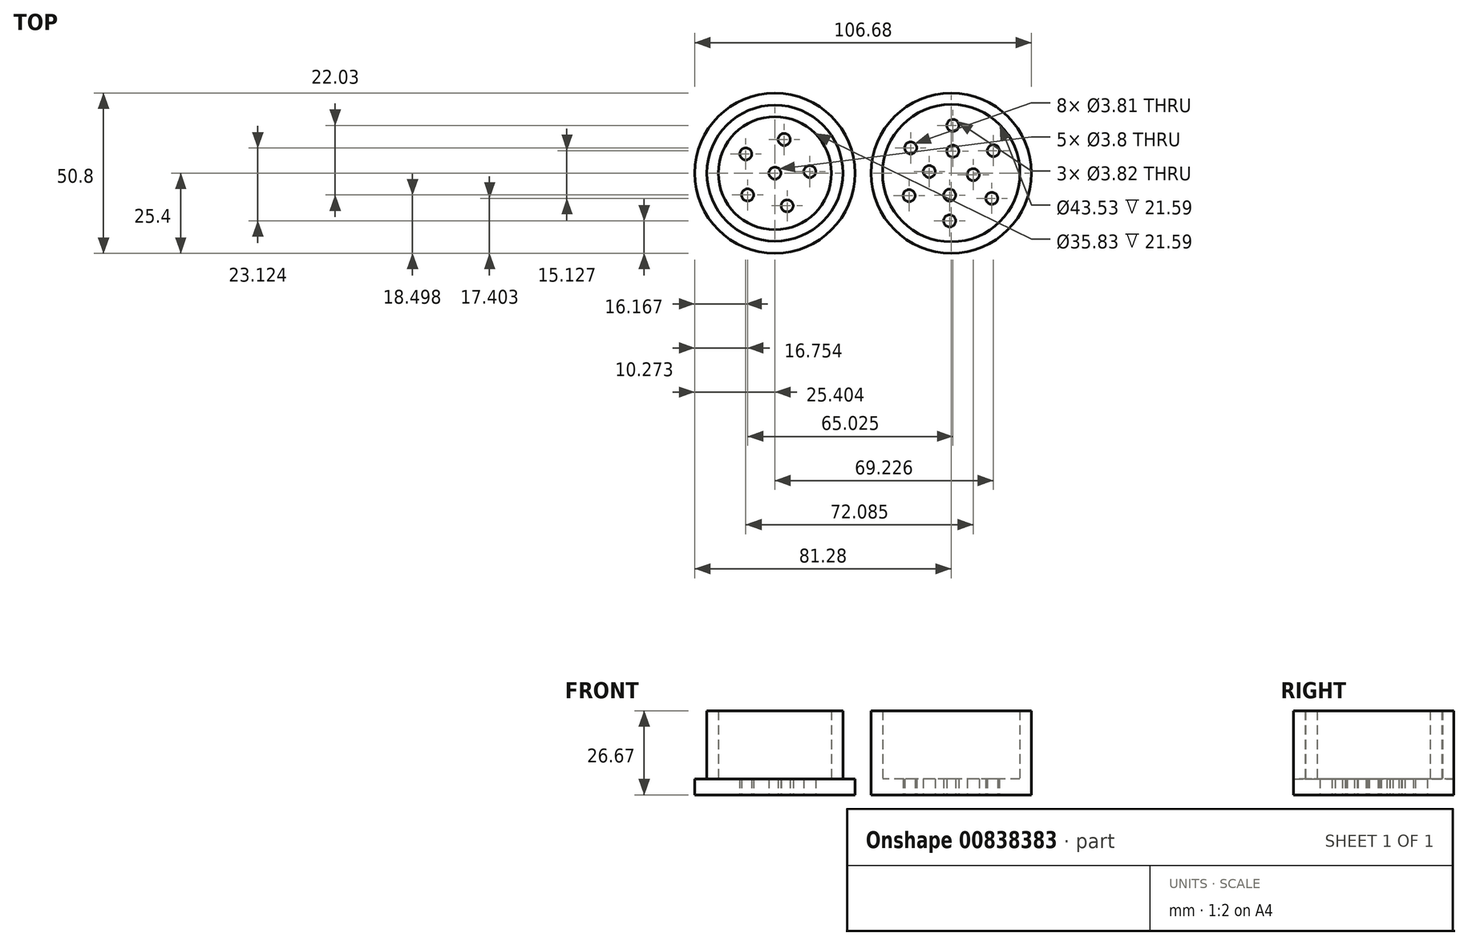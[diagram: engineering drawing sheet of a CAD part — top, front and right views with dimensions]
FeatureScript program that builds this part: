
annotation { "Feature Type Name" : "Feature", "Feature Type Description" : "" }
export const myFeature = defineFeature(function(context is Context, id is Id, definition is map)
    precondition{}
    {
        {
            var Q0;
            Q0=qCreatedBy(makeId("Top.planeOp"),FACE);
            var sketch = newSketch(context, id + "F0", { "sketchPlane" : qUnion([Q0])});
            skCircle(sketch, "E0", {"center": v(0, 0) * mm, "radius": 25.4 * mm});
            skCircle(sketch, "E1", {"center": v(0, 0) * mm, "radius": 21.77 * mm});
            skCircle(sketch, "E2", {"center": v(0, 0) * mm, "radius": 15.14 * mm});
            skCircle(sketch, "E3.cCircle", {"center": v(0, 0) * mm, "radius": 15.14 * mm, "construction": true});
            skLineSegment(sketch, "E3.0", {"start": v(0.5, 15.13) * mm, "end": v(13.35, 7.13) * mm});
            skLineSegment(sketch, "E3.1", {"start": v(13.35, 7.13) * mm, "end": v(12.85, -8) * mm});
            skLineSegment(sketch, "E3.2", {"start": v(12.85, -8) * mm, "end": v(-0.5, -15.13) * mm});
            skLineSegment(sketch, "E3.3", {"start": v(-0.5, -15.13) * mm, "end": v(-13.35, -7.13) * mm});
            skLineSegment(sketch, "E3.4", {"start": v(-13.35, -7.13) * mm, "end": v(-12.85, 8) * mm});
            skLineSegment(sketch, "E3.5", {"start": v(-12.85, 8) * mm, "end": v(0.5, 15.13) * mm});
            skCircle(sketch, "E4", {"center": v(0.5, 15.13) * mm, "radius": 1.9 * mm});
            skCircle(sketch, "E5", {"center": v(-12.85, 8) * mm, "radius": 1.9 * mm});
            skCircle(sketch, "E6", {"center": v(-13.35, -7.13) * mm, "radius": 1.9 * mm});
            skCircle(sketch, "E7", {"center": v(-0.5, -15.13) * mm, "radius": 1.9 * mm});
            skCircle(sketch, "E8", {"center": v(12.85, -8) * mm, "radius": 1.9 * mm});
            skCircle(sketch, "E9", {"center": v(13.35, 7.13) * mm, "radius": 1.9 * mm});
            skCircle(sketch, "E10", {"center": v(-55.88, 0) * mm, "radius": 25.4 * mm});
            skCircle(sketch, "E11", {"center": v(-55.88, 0) * mm, "radius": 21.57 * mm});
            skCircle(sketch, "E12", {"center": v(-55.88, 0) * mm, "radius": 17.92 * mm});
            skCircle(sketch, "E13", {"center": v(0, 0) * mm, "radius": 17.04 * mm});
            skCircle(sketch, "E14", {"center": v(0, 0) * mm, "radius": 6.99 * mm});
            skCircle(sketch, "E15.cCircle", {"center": v(0, 0) * mm, "radius": 6.99 * mm, "construction": true});
            skLineSegment(sketch, "E15.0", {"start": v(0.5, 6.97) * mm, "end": v(6.97, -0.5) * mm});
            skLineSegment(sketch, "E15.1", {"start": v(6.97, -0.5) * mm, "end": v(-0.5, -6.97) * mm});
            skLineSegment(sketch, "E15.2", {"start": v(-0.5, -6.97) * mm, "end": v(-6.97, 0.5) * mm});
            skLineSegment(sketch, "E15.3", {"start": v(-6.97, 0.5) * mm, "end": v(0.5, 6.97) * mm});
            skCircle(sketch, "E16", {"center": v(0.5, 6.97) * mm, "radius": 1.9 * mm});
            skCircle(sketch, "E17", {"center": v(6.97, -0.5) * mm, "radius": 1.9 * mm});
            skCircle(sketch, "E18", {"center": v(-0.5, -6.97) * mm, "radius": 1.9 * mm});
            skCircle(sketch, "E19", {"center": v(-6.97, 0.5) * mm, "radius": 1.9 * mm});
            skCircle(sketch, "E20", {"center": v(-55.88, 0) * mm, "radius": 11.07 * mm});
            skCircle(sketch, "E21.cCircle", {"center": v(-55.88, 0) * mm, "radius": 11.07 * mm, "construction": true});
            skLineSegment(sketch, "E21.0", {"start": v(-44.82, 0.5) * mm, "end": v(-51.98, -10.36) * mm});
            skLineSegment(sketch, "E21.1", {"start": v(-51.98, -10.36) * mm, "end": v(-64.53, -6.9) * mm});
            skLineSegment(sketch, "E21.2", {"start": v(-64.53, -6.9) * mm, "end": v(-65.11, 6.1) * mm});
            skLineSegment(sketch, "E21.3", {"start": v(-65.11, 6.1) * mm, "end": v(-52.93, 10.67) * mm});
            skLineSegment(sketch, "E21.4", {"start": v(-52.93, 10.67) * mm, "end": v(-44.82, 0.5) * mm});
            skCircle(sketch, "E22", {"center": v(-64.53, -6.9) * mm, "radius": 1.9 * mm});
            skCircle(sketch, "E23", {"center": v(-51.98, -10.36) * mm, "radius": 1.9 * mm});
            skCircle(sketch, "E24", {"center": v(-44.82, 0.5) * mm, "radius": 1.9 * mm});
            skCircle(sketch, "E25", {"center": v(-52.93, 10.67) * mm, "radius": 1.91 * mm});
            skCircle(sketch, "E26", {"center": v(-65.11, 6.1) * mm, "radius": 1.9 * mm});
            skCircle(sketch, "E27", {"center": v(-55.88, 0) * mm, "radius": 1.9 * mm});
            skSolve(sketch);
        }
        {
            var Q0;
            Q0=makeQuery(id+"F0.imprint","IMPRINT",FACE,{"disambiguationData":[TD([[makeQuery(id+"F0.imprint","IMPRINT",EDGE,{"derivedFrom":sQuery(id+"F0.wireOp",EDGE,"E10")}),1.0]])]});
            var Q1;
            Q1=makeQuery(id+"F0.imprint","IMPRINT",FACE,{"disambiguationData":[TD([[makeQuery(id+"F0.imprint","IMPRINT",EDGE,{"derivedFrom":sQuery(id+"F0.wireOp",EDGE,"E12")}),1.0]])]});
            var Q2;
            Q2=makeQuery(id+"F0.imprint","IMPRINT",FACE,{"disambiguationData":[TD([[makeQuery(id+"F0.imprint","IMPRINT",EDGE,{"derivedFrom":sQuery(id+"F0.wireOp",EDGE,"E1")}),1.0]])]});
            var Q3;
            {var subQ4=sQuery(id+"F0.wireOp",EDGE,"E13");Q3=makeQuery(id+"F0.imprint","IMPRINT",FACE,{"disambiguationData":[TD([[makeQuery(id+"F0.imprint","IMPRINT",EDGE,{"derivedFrom":subQ4}),1.0]])]});}
            var Q4;
            {var subQ0=sQuery(id+"F0.wireOp",EDGE,"E5");var subQ1=sQuery(id+"F0.wireOp",EDGE,"E2");var subQ2=makeQuery(id+"F0.imprint","INTERSECT",VERTEX,{"disambiguationData":[OD(1.0)],"derivedFrom":[subQ1,subQ0]});Q4=makeQuery(id+"F0.imprint","IMPRINT",FACE,{"disambiguationData":[TD([[makeQuery(id+"F0.imprint","IMPRINT",EDGE,{"disambiguationData":[TD([[subQ2,-1.0]])],"derivedFrom":subQ1}),1.0]])]});}
            var Q5;
            {var subQ0=sQuery(id+"F0.wireOp",EDGE,"E4");var subQ1=sQuery(id+"F0.wireOp",EDGE,"E2");var subQ2=makeQuery(id+"F0.imprint","INTERSECT",VERTEX,{"disambiguationData":[OD(1.0)],"derivedFrom":[subQ1,subQ0]});Q5=makeQuery(id+"F0.imprint","IMPRINT",FACE,{"disambiguationData":[TD([[makeQuery(id+"F0.imprint","IMPRINT",EDGE,{"disambiguationData":[TD([[subQ2,-1.0]])],"derivedFrom":subQ1}),1.0]])]});}
            var Q6;
            {var subQ15=sQuery(id+"F0.wireOp",EDGE,"E4");var subQ16=sQuery(id+"F0.wireOp",EDGE,"E3.0");var subQ17=makeQuery(id+"F0.imprint","INTERSECT",VERTEX,{"derivedFrom":[subQ16,subQ15]});Q6=makeQuery(id+"F0.imprint","IMPRINT",FACE,{"disambiguationData":[TD([[makeQuery(id+"F0.imprint","IMPRINT",EDGE,{"disambiguationData":[TD([[subQ17,-1.0]])],"derivedFrom":subQ16}),-1.0]])]});}
            var Q7;
            {var subQ0=sQuery(id+"F0.wireOp",EDGE,"E9");var subQ1=sQuery(id+"F0.wireOp",EDGE,"E2");var subQ2=makeQuery(id+"F0.imprint","INTERSECT",VERTEX,{"disambiguationData":[OD(0.0)],"derivedFrom":[subQ1,subQ0]});Q7=makeQuery(id+"F0.imprint","IMPRINT",FACE,{"disambiguationData":[TD([[makeQuery(id+"F0.imprint","IMPRINT",EDGE,{"disambiguationData":[TD([[subQ2,1.0]])],"derivedFrom":subQ1}),1.0]])]});}
            var Q8;
            {var subQ0=sQuery(id+"F0.wireOp",EDGE,"E9");var subQ1=sQuery(id+"F0.wireOp",EDGE,"E2");var subQ2=makeQuery(id+"F0.imprint","INTERSECT",VERTEX,{"disambiguationData":[OD(1.0)],"derivedFrom":[subQ1,subQ0]});Q8=makeQuery(id+"F0.imprint","IMPRINT",FACE,{"disambiguationData":[TD([[makeQuery(id+"F0.imprint","IMPRINT",EDGE,{"disambiguationData":[TD([[subQ2,-1.0]])],"derivedFrom":subQ1}),1.0]])]});}
            var Q9;
            {var subQ0=sQuery(id+"F0.wireOp",EDGE,"E6");var subQ1=sQuery(id+"F0.wireOp",EDGE,"E2");var subQ2=makeQuery(id+"F0.imprint","INTERSECT",VERTEX,{"disambiguationData":[OD(1.0)],"derivedFrom":[subQ1,subQ0]});Q9=makeQuery(id+"F0.imprint","IMPRINT",FACE,{"disambiguationData":[TD([[makeQuery(id+"F0.imprint","IMPRINT",EDGE,{"disambiguationData":[TD([[subQ2,-1.0]])],"derivedFrom":subQ1}),1.0]])]});}
            var Q10;
            {var subQ0=sQuery(id+"F0.wireOp",EDGE,"E7");var subQ1=sQuery(id+"F0.wireOp",EDGE,"E2");var subQ2=makeQuery(id+"F0.imprint","INTERSECT",VERTEX,{"disambiguationData":[OD(1.0)],"derivedFrom":[subQ1,subQ0]});Q10=makeQuery(id+"F0.imprint","IMPRINT",FACE,{"disambiguationData":[TD([[makeQuery(id+"F0.imprint","IMPRINT",EDGE,{"disambiguationData":[TD([[subQ2,-1.0]])],"derivedFrom":subQ1}),1.0]])]});}
            var Q11;
            {var subQ0=sQuery(id+"F0.wireOp",EDGE,"E18");var subQ1=sQuery(id+"F0.wireOp",EDGE,"E14");var subQ2=makeQuery(id+"F0.imprint","INTERSECT",VERTEX,{"disambiguationData":[OD(1.0)],"derivedFrom":[subQ1,subQ0]});Q11=makeQuery(id+"F0.imprint","IMPRINT",FACE,{"disambiguationData":[TD([[makeQuery(id+"F0.imprint","IMPRINT",EDGE,{"disambiguationData":[TD([[subQ2,-1.0]])],"derivedFrom":subQ1}),1.0]])]});}
            var Q12;
            {var subQ0=sQuery(id+"F0.wireOp",EDGE,"E19");var subQ1=sQuery(id+"F0.wireOp",EDGE,"E14");var subQ2=makeQuery(id+"F0.imprint","INTERSECT",VERTEX,{"disambiguationData":[OD(1.0)],"derivedFrom":[subQ1,subQ0]});Q12=makeQuery(id+"F0.imprint","IMPRINT",FACE,{"disambiguationData":[TD([[makeQuery(id+"F0.imprint","IMPRINT",EDGE,{"disambiguationData":[TD([[subQ2,-1.0]])],"derivedFrom":subQ1}),1.0]])]});}
            var Q13;
            {var subQ0=sQuery(id+"F0.wireOp",EDGE,"E16");var subQ1=sQuery(id+"F0.wireOp",EDGE,"E14");var subQ2=makeQuery(id+"F0.imprint","INTERSECT",VERTEX,{"disambiguationData":[OD(1.0)],"derivedFrom":[subQ1,subQ0]});Q13=makeQuery(id+"F0.imprint","IMPRINT",FACE,{"disambiguationData":[TD([[makeQuery(id+"F0.imprint","IMPRINT",EDGE,{"disambiguationData":[TD([[subQ2,-1.0]])],"derivedFrom":subQ1}),1.0]])]});}
            var Q14;
            {var subQ0=sQuery(id+"F0.wireOp",EDGE,"E16");var subQ1=sQuery(id+"F0.wireOp",EDGE,"E14");var subQ2=makeQuery(id+"F0.imprint","INTERSECT",VERTEX,{"disambiguationData":[OD(0.0)],"derivedFrom":[subQ1,subQ0]});Q14=makeQuery(id+"F0.imprint","IMPRINT",FACE,{"disambiguationData":[TD([[makeQuery(id+"F0.imprint","IMPRINT",EDGE,{"disambiguationData":[TD([[subQ2,1.0]])],"derivedFrom":subQ1}),1.0]])]});}
            var Q15;
            {var subQ3=sQuery(id+"F0.wireOp",EDGE,"E16");var subQ13=sQuery(id+"F0.wireOp",EDGE,"E15.0");var subQ14=makeQuery(id+"F0.imprint","INTERSECT",VERTEX,{"derivedFrom":[subQ13,subQ3]});Q15=makeQuery(id+"F0.imprint","IMPRINT",FACE,{"disambiguationData":[TD([[makeQuery(id+"F0.imprint","IMPRINT",EDGE,{"disambiguationData":[TD([[subQ14,-1.0]])],"derivedFrom":subQ13}),-1.0]])]});}
            var Q16;
            Q16=makeQuery(id+"F0.imprint","IMPRINT",FACE,{"disambiguationData":[TD([[makeQuery(id+"F0.imprint","IMPRINT",EDGE,{"derivedFrom":sQuery(id+"F0.wireOp",EDGE,"E27")}),-1.0]])]});
            var Q17;
            {var subQ0=sQuery(id+"F0.wireOp",EDGE,"E25");var subQ1=sQuery(id+"F0.wireOp",EDGE,"E20");var subQ2=makeQuery(id+"F0.imprint","INTERSECT",VERTEX,{"disambiguationData":[OD(1.0)],"derivedFrom":[subQ1,subQ0]});Q17=makeQuery(id+"F0.imprint","IMPRINT",FACE,{"disambiguationData":[TD([[makeQuery(id+"F0.imprint","IMPRINT",EDGE,{"disambiguationData":[TD([[subQ2,-1.0]])],"derivedFrom":subQ1}),1.0]])]});}
            var Q18;
            {var subQ0=sQuery(id+"F0.wireOp",EDGE,"E24");var subQ1=sQuery(id+"F0.wireOp",EDGE,"E20");var subQ2=makeQuery(id+"F0.imprint","INTERSECT",VERTEX,{"disambiguationData":[OD(0.0)],"derivedFrom":[subQ1,subQ0]});Q18=makeQuery(id+"F0.imprint","IMPRINT",FACE,{"disambiguationData":[TD([[makeQuery(id+"F0.imprint","IMPRINT",EDGE,{"disambiguationData":[TD([[subQ2,-1.0]])],"derivedFrom":subQ1}),1.0]])]});}
            var Q19;
            {var subQ0=sQuery(id+"F0.wireOp",EDGE,"E23");var subQ1=sQuery(id+"F0.wireOp",EDGE,"E20");var subQ2=makeQuery(id+"F0.imprint","INTERSECT",VERTEX,{"disambiguationData":[OD(1.0)],"derivedFrom":[subQ1,subQ0]});Q19=makeQuery(id+"F0.imprint","IMPRINT",FACE,{"disambiguationData":[TD([[makeQuery(id+"F0.imprint","IMPRINT",EDGE,{"disambiguationData":[TD([[subQ2,-1.0]])],"derivedFrom":subQ1}),1.0]])]});}
            var Q20;
            {var subQ0=sQuery(id+"F0.wireOp",EDGE,"E22");var subQ1=sQuery(id+"F0.wireOp",EDGE,"E20");var subQ2=makeQuery(id+"F0.imprint","INTERSECT",VERTEX,{"disambiguationData":[OD(1.0)],"derivedFrom":[subQ1,subQ0]});Q20=makeQuery(id+"F0.imprint","IMPRINT",FACE,{"disambiguationData":[TD([[makeQuery(id+"F0.imprint","IMPRINT",EDGE,{"disambiguationData":[TD([[subQ2,-1.0]])],"derivedFrom":subQ1}),1.0]])]});}
            var Q21;
            {var subQ0=sQuery(id+"F0.wireOp",EDGE,"E26");var subQ1=sQuery(id+"F0.wireOp",EDGE,"E20");var subQ2=makeQuery(id+"F0.imprint","INTERSECT",VERTEX,{"disambiguationData":[OD(1.0)],"derivedFrom":[subQ1,subQ0]});Q21=makeQuery(id+"F0.imprint","IMPRINT",FACE,{"disambiguationData":[TD([[makeQuery(id+"F0.imprint","IMPRINT",EDGE,{"disambiguationData":[TD([[subQ2,-1.0]])],"derivedFrom":subQ1}),1.0]])]});}
            extrude(context, id + "F1", {"entities" : qUnion([Q0, Q1, Q2, Q3, Q4, Q5, Q6, Q7, Q8, Q9, Q10, Q11, Q12, Q13, Q14, Q15, Q16, Q17, Q18, Q19, Q20, Q21]), "depth" : 5.08 * mm, "offsetDistance" : 25.4 * mm});
        }
        {
            var Q0;
            Q0=makeQuery(id+"F0.imprint","IMPRINT",FACE,{"disambiguationData":[TD([[makeQuery(id+"F0.imprint","IMPRINT",EDGE,{"derivedFrom":sQuery(id+"F0.wireOp",EDGE,"E11")}),1.0]])]});
            var Q1;
            Q1=makeQuery(id+"F0.imprint","IMPRINT",FACE,{"disambiguationData":[TD([[makeQuery(id+"F0.imprint","IMPRINT",EDGE,{"derivedFrom":sQuery(id+"F0.wireOp",EDGE,"E0")}),1.0]])]});
            extrude(context, id + "F2", {"entities" : qUnion([Q0, Q1]), "operationType" : NewBodyOperationType.ADD, "depth" : 26.67 * mm, "offsetDistance" : 25.4 * mm});
        }
    });
